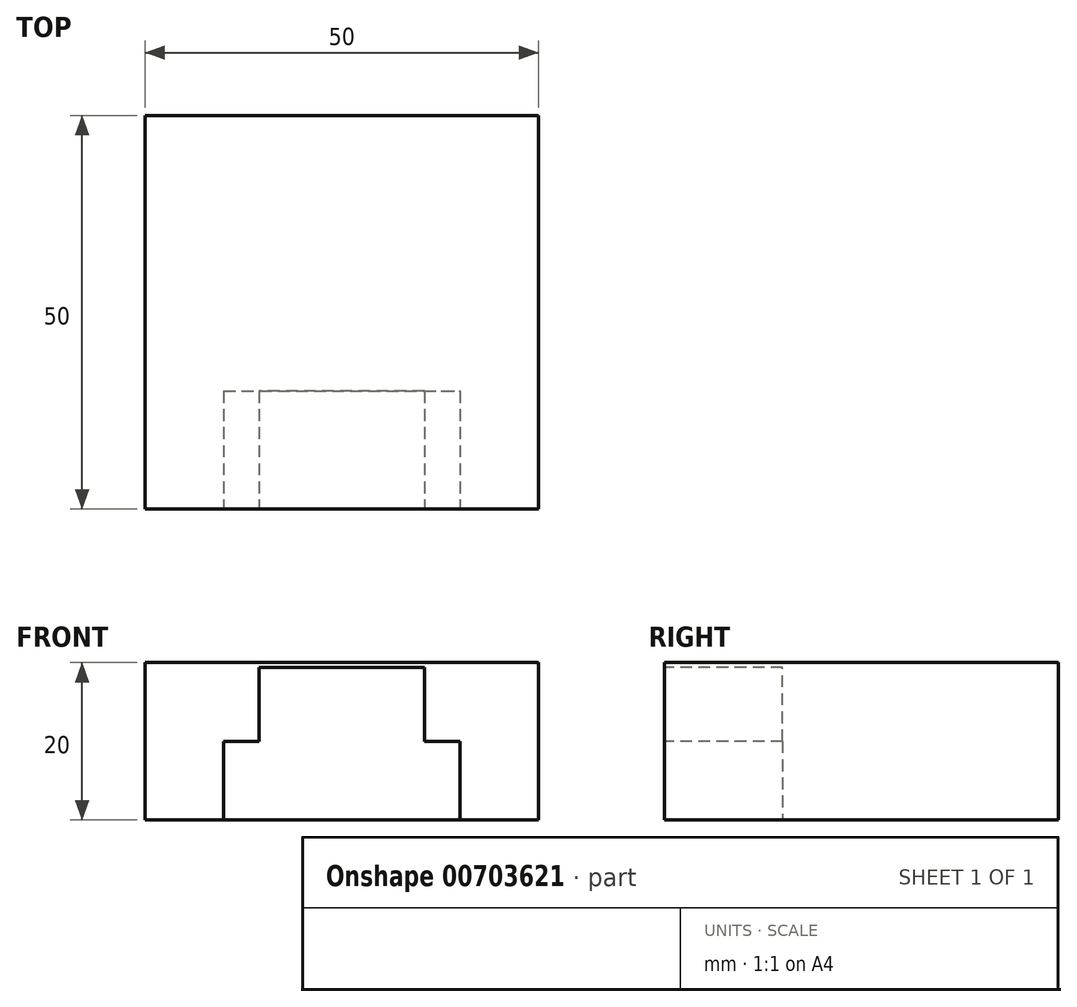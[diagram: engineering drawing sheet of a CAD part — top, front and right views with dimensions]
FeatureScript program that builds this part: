
annotation { "Feature Type Name" : "Feature", "Feature Type Description" : "" }
export const myFeature = defineFeature(function(context is Context, id is Id, definition is map)
    precondition{}
    {
        {
            var Q0;
            Q0=qCreatedBy(makeId("Top.planeOp"),FACE);
            var sketch = newSketch(context, id + "F0", { "sketchPlane" : qUnion([Q0])});
            skLineSegment(sketch, "E0.bottom", {"start": v(25, 25) * mm, "end": v(-25, 25) * mm});
            skLineSegment(sketch, "E0.top", {"start": v(25, -25) * mm, "end": v(-25, -25) * mm});
            skLineSegment(sketch, "E0.left", {"start": v(25, 25) * mm, "end": v(25, -25) * mm});
            skLineSegment(sketch, "E0.right", {"start": v(-25, 25) * mm, "end": v(-25, -25) * mm});
            skPoint(sketch, "E0.middle", {"position": v(0, 0) * mm});
            skSolve(sketch);
        }
        {
            var Q0;
            Q0=makeQuery(id+"F0.imprint","IMPRINT",FACE,{"disambiguationData":[TD([[makeQuery(id+"F0.imprint","IMPRINT",EDGE,{"derivedFrom":sQuery(id+"F0.wireOp",EDGE,"E0.bottom")}),1.0]])]});
            extrude(context, id + "F1", {"entities" : qUnion([Q0]), "depth" : 20 * mm, "offsetDistance" : 25 * mm});
        }
        {
            var Q0;
            Q0=makeQuery(id+"F1.opExtrude","SWEPT_FACE",FACE,{"disambiguationData":[OSD([sQuery(id+"F0.wireOp",EDGE,"E0.top")])]});
            var sketch = newSketch(context, id + "F2", { "sketchPlane" : qUnion([Q0])});
            skLineSegment(sketch, "E1.bottom", {"start": v(15, 16) * mm, "end": v(-15, 16) * mm});
            skLineSegment(sketch, "E1.top", {"start": v(15, 4) * mm, "end": v(-15, 4) * mm});
            skLineSegment(sketch, "E1.left", {"start": v(15, 16) * mm, "end": v(15, 4) * mm});
            skLineSegment(sketch, "E1.right", {"start": v(-15, 16) * mm, "end": v(-15, 4) * mm});
            skPoint(sketch, "E1.middle", {"position": v(0, 10) * mm});
            skPoint(sketch, "E1.middle.positionSnap0", {"position": v(-25, 10) * mm});
            skPoint(sketch, "E1.middle.positionSnap1", {"position": v(0, 0) * mm});
            skPoint(sketch, "E1.centerSnap0", {"position": v(-25, 10) * mm});
            skPoint(sketch, "E1.centerSnap1", {"position": v(0, 0) * mm});
            skLineSegment(sketch, "E2", {"start": v(-15, 10) * mm, "end": v(15, 10) * mm});
            skLineSegment(sketch, "E3", {"start": v(10.5, 10) * mm, "end": v(10.5, 4) * mm});
            skLineSegment(sketch, "E4", {"start": v(-10.5, 10) * mm, "end": v(-10.5, 4) * mm});
            skLineSegment(sketch, "E5", {"start": v(-10.5, 10) * mm, "end": v(-10.5, 16) * mm});
            skLineSegment(sketch, "E6", {"start": v(10.5, 10) * mm, "end": v(10.5, 16) * mm});
            skPoint(sketch, "E6.endSnap0", {"position": v(0, 16) * mm});
            skSolve(sketch);
        }
        {
            var Q0;
            {var subQ3=sQuery(id+"F2.wireOp",EDGE,"E4");Q0=makeQuery(id+"F2.imprint","IMPRINT",FACE,{"disambiguationData":[TD([[makeQuery(id+"F2.imprint","IMPRINT",EDGE,{"derivedFrom":subQ3}),-1.0]])]});}
            var Q1;
            {var subQ3=sQuery(id+"F2.wireOp",EDGE,"E3");Q1=makeQuery(id+"F2.imprint","IMPRINT",FACE,{"disambiguationData":[TD([[makeQuery(id+"F2.imprint","IMPRINT",EDGE,{"derivedFrom":subQ3}),1.0]])]});}
            var Q2;
            {var subQ0=sQuery(id+"F2.wireOp",EDGE,"E3");Q2=makeQuery(id+"F2.imprint","IMPRINT",FACE,{"disambiguationData":[TD([[makeQuery(id+"F2.imprint","IMPRINT",EDGE,{"derivedFrom":subQ0}),-1.0]])]});}
            extrude(context, id + "F3", {"entities" : qUnion([Q0, Q1, Q2]), "operationType" : NewBodyOperationType.ADD, "depth" : 10 * mm, "offsetDistance" : 25 * mm});
        }
        {
            var Q0;
            {var subQ0=sQuery(id+"F2.wireOp",EDGE,"E5");Q0=makeQuery(id+"F2.imprint","IMPRINT",FACE,{"disambiguationData":[TD([[makeQuery(id+"F2.imprint","IMPRINT",EDGE,{"derivedFrom":subQ0}),-1.0]])]});}
            extrude(context, id + "F4", {"entities" : qUnion([Q0]), "operationType" : NewBodyOperationType.ADD, "depth" : 10 * mm, "offsetDistance" : 25 * mm});
        }
        {
            var Q0;
            Q0=makeQuery(id+"F4.opExtrude","SWEPT_FACE",FACE,{"disambiguationData":[OSD([sQuery(id+"F2.wireOp",EDGE,"E1.bottom")])]});
            extrude(context, id + "F5", {"entities" : qUnion([Q0]), "operationType" : NewBodyOperationType.ADD, "depth" : 3.4 * mm, "offsetDistance" : 25 * mm});
        }
        {
            var Q0;
            Q0=makeQuery(id+"F1.opExtrude","SWEPT_BODY",BODY,{"disambiguationData":[OSD([sQuery(id+"F0.wireOp",EDGE,"E0.bottom"),sQuery(id+"F0.wireOp",EDGE,"E0.top"),sQuery(id+"F0.wireOp",EDGE,"E0.left"),sQuery(id+"F0.wireOp",EDGE,"E0.right")])]});
            transform(context, id + "F6", {"entities" : qUnion([Q0]), "transformType" : TransformType.TRANSLATION_3D, "dx" : 0 * mm, "dy" : 0 * mm, "dz" : 0 * mm, "makeCopy" : true});
        }
        {
            var Q0;
            Q0=makeQuery(id+"F6.opPattern","COPY",FACE,{"derivedFrom":makeQuery(id+"F3.opExtrude","SWEPT_FACE",FACE,{"disambiguationData":[OSD([sQuery(id+"F2.wireOp",EDGE,"E1.top")])]}),"instanceName":"1"});
            extrude(context, id + "F7", {"entities" : qUnion([Q0]), "operationType" : NewBodyOperationType.ADD, "depth" : 7.7 * mm, "offsetDistance" : 25 * mm});
        }
        {
            var Q0;
            {var subQ0=sQuery(id+"F2.wireOp",EDGE,"E1.top");var subQ1=sQuery(id+"F2.wireOp",EDGE,"E1.bottom");var subQ2=sQuery(id+"F2.wireOp",EDGE,"E2");Q0=makeQuery(id+"F7.boolean.opBoolean","MERGE",FACE,{"derivedFrom":[makeQuery(id+"F6.opPattern","COPY",FACE,{"derivedFrom":makeQuery(id+"F5.boolean.opBoolean","MERGE",FACE,{"derivedFrom":[makeQuery(id+"F4.boolean.opBoolean","MERGE",FACE,{"derivedFrom":[makeQuery(id+"F3.opExtrude","CAP_FACE",FACE,{"disambiguationData":[OSD([subQ0,sQuery(id+"F2.wireOp",EDGE,"E1.left"),sQuery(id+"F2.wireOp",EDGE,"E1.right"),subQ2])],"isStart":false}),makeQuery(id+"F4.opExtrude","CAP_FACE",FACE,{"disambiguationData":[OSD([subQ1,subQ2,sQuery(id+"F2.wireOp",EDGE,"E5"),sQuery(id+"F2.wireOp",EDGE,"E6")])],"isStart":false})]}),makeQuery(id+"F5.opExtrude","SWEPT_FACE",FACE,{"disambiguationData":[OSD([subQ1]),TDD([makeQuery(id+"F4.opExtrude","CAP_EDGE",EDGE,{"disambiguationData":[OSD([subQ1])],"isStart":false})])]})]}),"instanceName":"1"}),makeQuery(id+"F7.opExtrude","SWEPT_FACE",FACE,{"disambiguationData":[OSD([subQ0]),TDD([makeQuery(id+"F6.opPattern","COPY",EDGE,{"derivedFrom":makeQuery(id+"F3.opExtrude","CAP_EDGE",EDGE,{"disambiguationData":[OSD([subQ0])],"isStart":false}),"instanceName":"1"})])]})]});}
            extrude(context, id + "F8", {"entities" : qUnion([Q0]), "operationType" : NewBodyOperationType.REMOVE, "oppositeDirection" : true, "depth" : 25 * mm, "offsetDistance" : 25 * mm});
        }
    });
